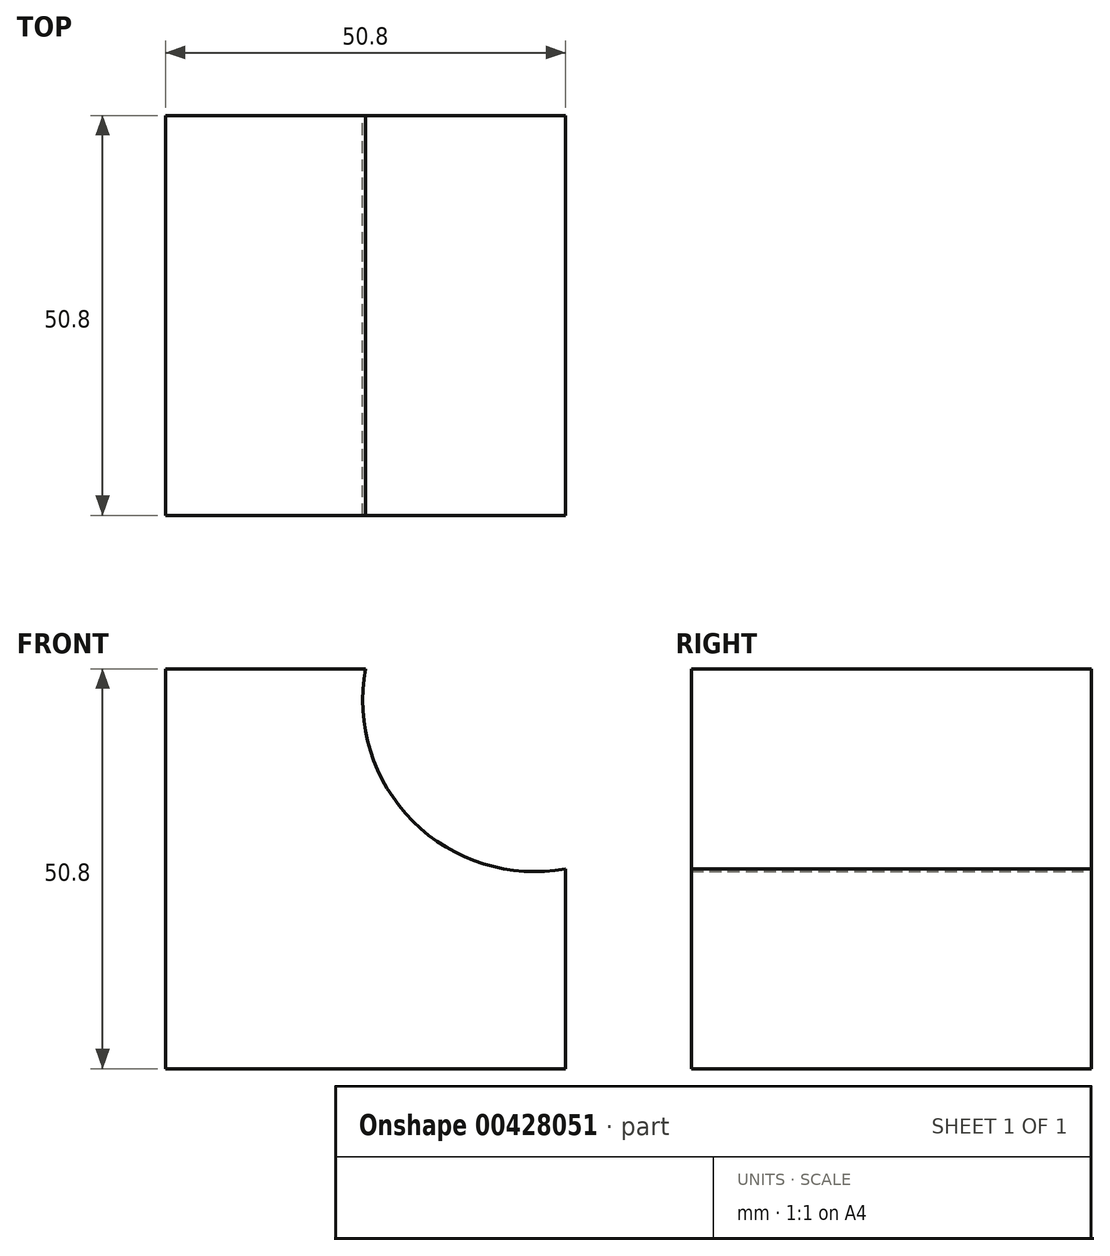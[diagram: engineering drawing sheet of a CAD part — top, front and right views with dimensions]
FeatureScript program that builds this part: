
annotation { "Feature Type Name" : "Feature", "Feature Type Description" : "" }
export const myFeature = defineFeature(function(context is Context, id is Id, definition is map)
    precondition{}
    {
        {
            var Q0;
            Q0=qCreatedBy(makeId("Front.planeOp"),FACE);
            var sketch = newSketch(context, id + "F0", { "sketchPlane" : qUnion([Q0])});
            skLineSegment(sketch, "E0", {"start": v(0, 0) * mm, "end": v(50.8, 0) * mm});
            skLineSegment(sketch, "E1", {"start": v(0, 0) * mm, "end": v(0, 50.8) * mm});
            skLineSegment(sketch, "E2", {"start": v(50.8, 0) * mm, "end": v(50.8, 25.4) * mm});
            skLineSegment(sketch, "E3", {"start": v(0, 50.8) * mm, "end": v(25.4, 50.8) * mm});
            skArc(sketch, "E4", {"start": v(25.4, 50.8) * mm, "mid": v(31.42, 31.42) * mm, "end": v(50.8, 25.4) * mm});
            skSolve(sketch);
        }
        {
            var Q0;
            Q0=makeQuery(id+"F0.imprint","IMPRINT",FACE,{"disambiguationData":[TD([[makeQuery(id+"F0.imprint","IMPRINT",EDGE,{"derivedFrom":sQuery(id+"F0.wireOp",EDGE,"E0")}),1.0]])]});
            extrude(context, id + "F1", {"entities" : qUnion([Q0]), "depth" : 50.8 * mm});
        }
    });
